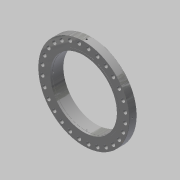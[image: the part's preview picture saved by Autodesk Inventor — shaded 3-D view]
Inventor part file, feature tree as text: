
AUTODESK INVENTOR PART (.ipt)
format: ipt  version: 2017.3 (Build 213257000, 257)  size: 392,192 bytes
history: native  units: in
note: dims shown in document units (in); Inventor stores cm internally (conversion verified against a paired STEP export)
features: sketch x6, hole x4, chamfer x4, extrude x3, pattern_circular x2, fillet x2, revolve x1, plane x1, projected_geometry x1
ambient origin geometry x8: Origin, YZ Plane, XZ Plane, XY Plane, X Axis, Y Axis, Z Axis, Center Point
bodies: Solid1 (feature_tree)
feature tree (24):
  extrude  "Extrusion1"  Depth=31.25in
  extrude  "Extrusion2"  Depth=33.75in
  extrude  "Extrusion3"  Depth=34.75in
  hole  "Hole1"  [1 undecoded]
  chamfer  "Chamfer3"  Distance=11.0236in Angle=360.0deg
  pattern_circular  "Circular Pattern1"  [2 undecoded]
  chamfer  "Chamfer2"  Distance=0.0312in Angle=45.0deg
  fillet  "Fillet2"  Radius=0.0625in
  chamfer  "Chamfer4"  Distance=0.2577in
  revolve  "Revolution1"  Angle=90.0deg
  fillet  "Fillet5"  Radius=0.25in
  chamfer  "Chamfer7"  Distance=0.6875in
  plane  "Work Plane1"
  sketch  "Sketch11"  dims[d25=0.0625in d26=0.125in d27=0.0687in d29=0.4375in d30=0.0312in d31=0.125in d32=45.0deg d33=0.0625in d34=0.125in d35=45.0deg d45=0.2577in d49=90.0deg d59=0.25in d69=0.6875in d70=0.125in d71=1.0in d72=15.75in d73=0.0312in d74=0.0312in d75=0.125in d76=45.0deg d96=17.0in d97=0.5in d98=1.0in d99=0.0442in d101=0.5in d102=0.688in d103=0.534in d104=0.0246in d105=0.688in d106=0.375in d107=0.25in d108=0.5635in d109=1.1in d110=0.8108in d111=0.417in d112=1.0in d113=0.375in d114=0.25in d115=0.5635in d116=1.75in d117=0.8108in d118=0.4062in d119=1.0in d120=0.375in d121=0.25in d122=0.5635in d123=6.0in d124=0.8108in d125=1.5748in d126=360.0deg]
  hole  "Hole4"  [1 undecoded]
  hole  "Hole5"  [1 undecoded]
  hole  "Hole6"  [1 undecoded]
  pattern_circular  "Circular Pattern3"  [2 undecoded]
  sketch  "Sketch1"  dims[d0=43.0in d1=31.25in]
  sketch  "Sketch2"  dims[d2=3.5625in d3=0.0in d4=33.75in]
  sketch  "Sketch3"  dims[d5=0.0625in d6=0.0in d7=34.75in]
  sketch  "Sketch4"  dims[d8=2.4375in d9=0.0in d13=19.625in]
  sketch  "Sketch6"  dims[d15=1.875in d16=0.75in d17=0.375in d18=0.25in d19=0.5635in d20=1.0in d21=0.8108in d22=11.0236in d23=360.0deg]
  projected_geometry  "Projected Loop1"
note: 8 required parameter values undecoded (feature->parameter linkage not recoverable at this tier; creation-order binding heuristic only, values carry confidence <= 0.55)
